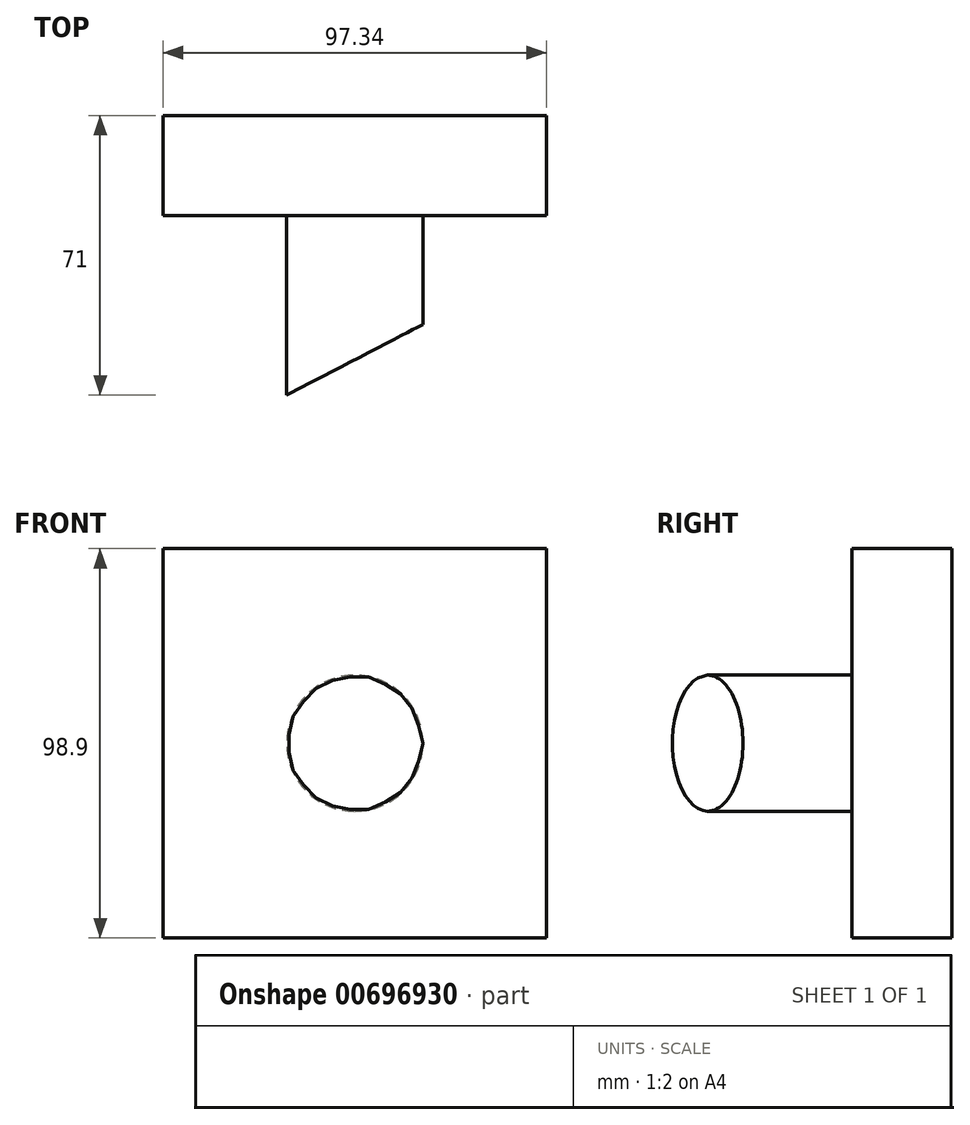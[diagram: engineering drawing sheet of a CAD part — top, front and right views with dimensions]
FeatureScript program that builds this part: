
annotation { "Feature Type Name" : "Feature", "Feature Type Description" : "" }
export const myFeature = defineFeature(function(context is Context, id is Id, definition is map)
    precondition{}
    {
        {
            var Q0;
            Q0=qCreatedBy(makeId("Front.planeOp"),FACE);
            var sketch = newSketch(context, id + "F0", { "sketchPlane" : qUnion([Q0])});
            skLineSegment(sketch, "E0.bottom", {"start": v(-48.67, -49.45) * mm, "end": v(48.67, -49.45) * mm});
            skLineSegment(sketch, "E0.top", {"start": v(-48.67, 49.45) * mm, "end": v(48.67, 49.45) * mm});
            skLineSegment(sketch, "E0.left", {"start": v(-48.67, -49.45) * mm, "end": v(-48.67, 49.45) * mm});
            skLineSegment(sketch, "E0.right", {"start": v(48.67, -49.45) * mm, "end": v(48.67, 49.45) * mm});
            skPoint(sketch, "E0.middle", {"position": v(0, 0) * mm});
            skSolve(sketch);
        }
        {
            var Q0;
            Q0 = qSketchRegion(id + "F0", true);
            extrude(context, id + "F1", {"entities" : qUnion([Q0]), "depth" : 25.4 * mm, "offsetDistance" : 25.4 * mm});
        }
        {
            var Q0;
            Q0=makeQuery(id+"F1.opExtrude","CAP_FACE",FACE,{"disambiguationData":[OSD([sQuery(id+"F0.wireOp",EDGE,"E0.bottom"),sQuery(id+"F0.wireOp",EDGE,"E0.top"),sQuery(id+"F0.wireOp",EDGE,"E0.left"),sQuery(id+"F0.wireOp",EDGE,"E0.right")])],"isStart":false});
            var sketch = newSketch(context, id + "F2", { "sketchPlane" : qUnion([Q0])});
            skCircle(sketch, "E1", {"center": v(0, 0) * mm, "radius": 17.29 * mm});
            skSolve(sketch);
        }
        {
            var Q0;
            Q0=makeQuery(id+"F2.imprint","IMPRINT",FACE,{"disambiguationData":[TD([[makeQuery(id+"F2.imprint","IMPRINT",EDGE,{"derivedFrom":sQuery(id+"F2.wireOp",EDGE,"E1")}),1.0]])]});
            extrude(context, id + "F3", {"entities" : qUnion([Q0]), "operationType" : NewBodyOperationType.ADD, "depth" : 50.8 * mm, "offsetDistance" : 25.4 * mm});
        }
        {
            var Q0;
            Q0=qCreatedBy(makeId("Top.planeOp"),FACE);
            var sketch = newSketch(context, id + "F4", { "sketchPlane" : qUnion([Q0])});
            skLineSegment(sketch, "E2", {"start": v(-35.25, -80.33) * mm, "end": v(48.69, -80.33) * mm});
            skLineSegment(sketch, "E3", {"start": v(48.69, -80.33) * mm, "end": v(48.69, -36.72) * mm});
            skLineSegment(sketch, "E4", {"start": v(48.69, -36.72) * mm, "end": v(-35.25, -80.33) * mm});
            skSolve(sketch);
        }
        {
            var Q0;
            Q0 = qSketchRegion(id + "F4", true);
            var Q1;
            Q1=makeQuery(id+"F4.imprint","IMPRINT",FACE,{"disambiguationData":[TD([[makeQuery(id+"F4.imprint","IMPRINT",EDGE,{"derivedFrom":sQuery(id+"F4.wireOp",EDGE,"E2")}),1.0]])]});
            extrude(context, id + "F5", {"entities" : qUnion([Q0, Q1]), "operationType" : NewBodyOperationType.REMOVE, "endBound" : BoundingType.SYMMETRIC, "oppositeDirection" : true, "depth" : 71.63 * mm, "offsetDistance" : 25.4 * mm});
        }
    });
